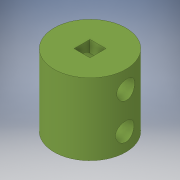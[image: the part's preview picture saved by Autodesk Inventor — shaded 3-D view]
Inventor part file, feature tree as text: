
AUTODESK INVENTOR PART (.ipt)
format: ipt  version: 2018 (Build 220112000, 112)  size: 144,384 bytes
history: native  units: in
note: dims shown in document units (in); Inventor stores cm internally (conversion verified against a paired STEP export)
features: extrude x3, sketch x3
ambient origin geometry x8: Origin, YZ Plane, XZ Plane, XY Plane, X Axis, Y Axis, Z Axis, Center Point
bodies: Solid1 (feature_tree)
feature tree (6):
  extrude  "Extrusion1"  Depth=0.75in
  extrude  "Extrusion2"  Depth=0.375in
  extrude  "Extrusion3"  Depth=0.1925in
  sketch  "Sketch1"  dims[d0=0.1675in d1=0.75in]
  sketch  "Sketch2"  dims[d2=0.375in d3=0.0in d4=0.375in]
  sketch  "Sketch3"  dims[d5=0.375in d6=0.0in d7=0.1925in d8=0.1925in d9=0.75in d10=0.0in]
